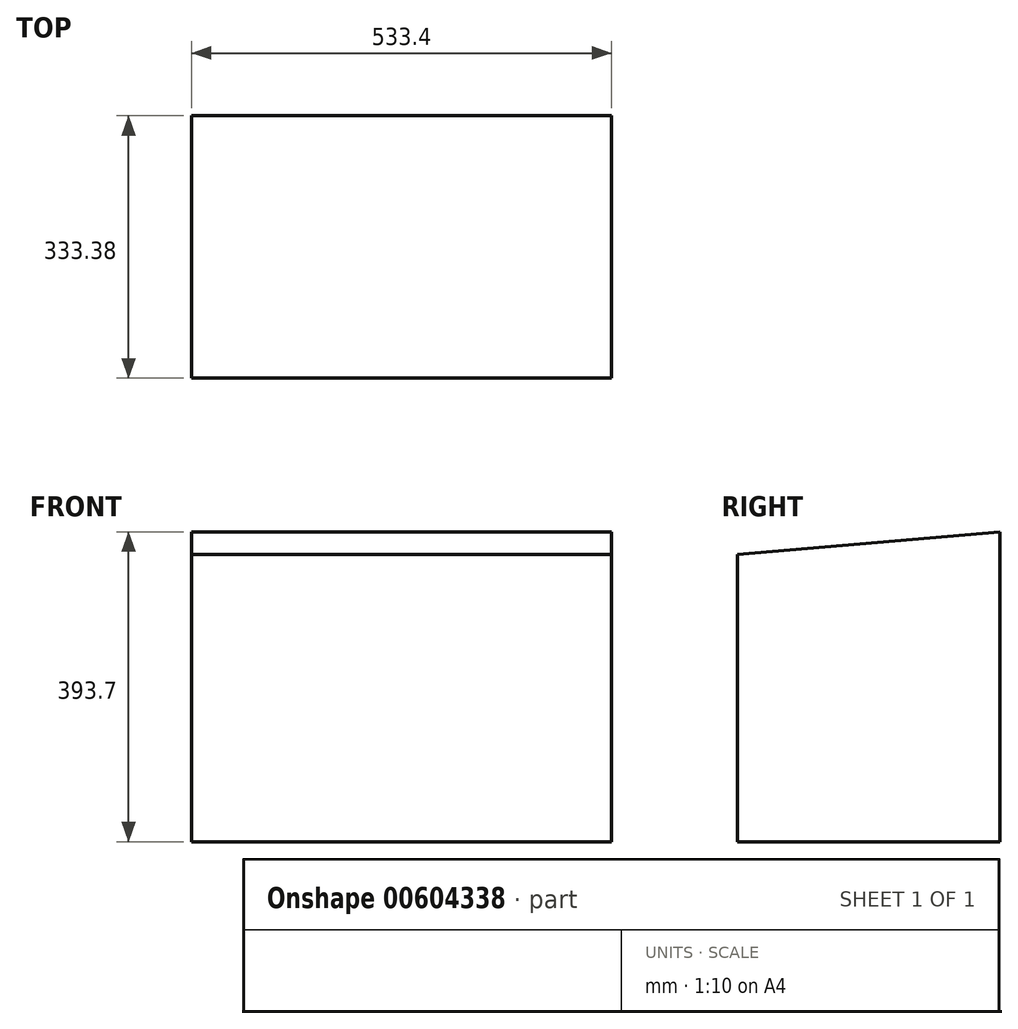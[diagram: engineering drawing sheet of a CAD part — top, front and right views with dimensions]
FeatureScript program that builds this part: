
annotation { "Feature Type Name" : "Feature", "Feature Type Description" : "" }
export const myFeature = defineFeature(function(context is Context, id is Id, definition is map)
    precondition{}
    {
        {
            var Q0;
            Q0=qCreatedBy(makeId("Right.planeOp"),FACE);
            var sketch = newSketch(context, id + "F0", { "sketchPlane" : qUnion([Q0])});
            skLineSegment(sketch, "E0", {"start": v(0, 0) * mm, "end": v(333.38, 0) * mm});
            skLineSegment(sketch, "E1", {"start": v(333.38, 0) * mm, "end": v(333.38, 393.7) * mm});
            skLineSegment(sketch, "E2", {"start": v(333.38, 393.7) * mm, "end": v(0, 365.12) * mm});
            skLineSegment(sketch, "E3", {"start": v(0, 365.13) * mm, "end": v(0, 0) * mm});
            skSolve(sketch);
        }
        {
            var Q0;
            Q0 = qSketchRegion(id + "F0", true);
            extrude(context, id + "F1", {"entities" : qUnion([Q0]), "endBound" : BoundingType.SYMMETRIC, "depth" : 533.4 * mm, "offsetDistance" : 25.4 * mm});
        }
    });
